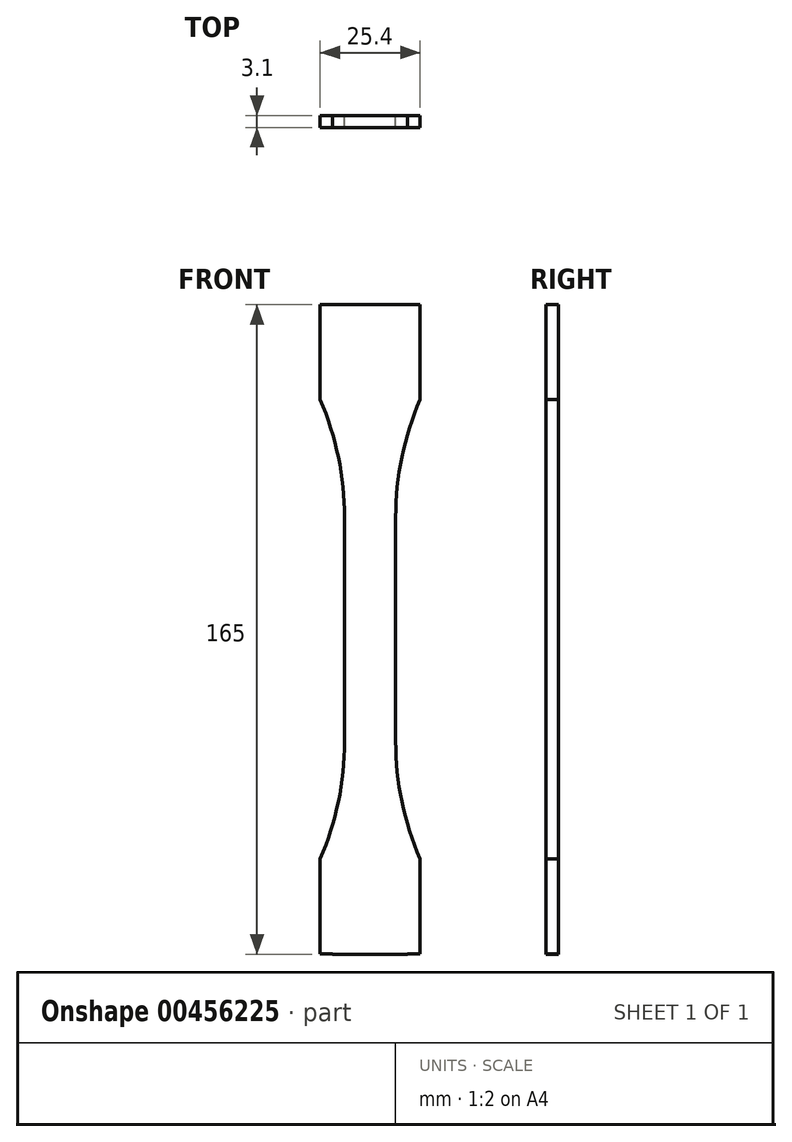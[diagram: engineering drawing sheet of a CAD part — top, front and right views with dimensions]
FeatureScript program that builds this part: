
annotation { "Feature Type Name" : "Feature", "Feature Type Description" : "" }
export const myFeature = defineFeature(function(context is Context, id is Id, definition is map)
    precondition{}
    {
        {
            var Q0;
            Q0=qCreatedBy(makeId("Front.planeOp"),FACE);
            var sketch = newSketch(context, id + "F0", { "sketchPlane" : qUnion([Q0])});
            skLineSegment(sketch, "E0.bottom", {"start": v(-6.5, 28.5) * mm, "end": v(0, 28.5) * mm});
            skLineSegment(sketch, "E0.top", {"start": v(-6.5, 0) * mm, "end": v(0, 0) * mm});
            skLineSegment(sketch, "E0.left", {"start": v(-6.5, 28.5) * mm, "end": v(-6.5, 0) * mm});
            skLineSegment(sketch, "E0.right", {"start": v(0, 28.5) * mm, "end": v(0, 0) * mm});
            skLineSegment(sketch, "E1", {"start": v(0, 28.5) * mm, "end": v(0, 49.5) * mm});
            skLineSegment(sketch, "E2.bottom", {"start": v(0, 49.5) * mm, "end": v(-9.5, 49.5) * mm});
            skLineSegment(sketch, "E2.top", {"start": v(0, 82.5) * mm, "end": v(-9.5, 82.5) * mm});
            skLineSegment(sketch, "E2.left", {"start": v(0, 49.5) * mm, "end": v(0, 82.5) * mm});
            skLineSegment(sketch, "E2.right", {"start": v(-9.5, 49.5) * mm, "end": v(-9.5, 49.5) * mm});
            skPoint(sketch, "E3.third.point", {"position": v(-81.94, 24.1) * mm});
            skPoint(sketch, "E4.third.point", {"position": v(-11.7, 28.5) * mm});
            skLineSegment(sketch, "E5", {"start": v(-9.5, 49.5) * mm, "end": v(-9.5, 82.5) * mm});
            skLineSegment(sketch, "E6.MirrorCS", {"start": v(9.5, 49.5) * mm, "end": v(9.5, 49.5) * mm});
            skLineSegment(sketch, "E7.MirrorCS", {"start": v(0, 82.5) * mm, "end": v(9.5, 82.5) * mm});
            skLineSegment(sketch, "E8.MirrorCS", {"start": v(6.5, 28.5) * mm, "end": v(6.5, 0) * mm});
            skLineSegment(sketch, "E9.MirrorCS", {"start": v(6.5, 28.5) * mm, "end": v(0, 28.5) * mm});
            skLineSegment(sketch, "E10.MirrorCS", {"start": v(0, 49.5) * mm, "end": v(0, 49.5) * mm});
            skLineSegment(sketch, "E11.MirrorCS", {"start": v(9.5, 49.5) * mm, "end": v(9.5, 82.5) * mm});
            skLineSegment(sketch, "E12.MirrorCS", {"start": v(6.5, 0) * mm, "end": v(0, 0) * mm});
            skLineSegment(sketch, "E13.MirrorCS", {"start": v(0, -28.5) * mm, "end": v(0, -49.5) * mm});
            skLineSegment(sketch, "E14.MirrorCS", {"start": v(0, -28.5) * mm, "end": v(0, 0) * mm});
            skLineSegment(sketch, "E15.MirrorCS", {"start": v(-9.5, -49.5) * mm, "end": v(-9.5, -49.5) * mm});
            skLineSegment(sketch, "E16.MirrorCS", {"start": v(0, -82.5) * mm, "end": v(9.5, -82.5) * mm});
            skLineSegment(sketch, "E17.MirrorCS", {"start": v(0, -49.5) * mm, "end": v(9.5, -49.5) * mm});
            skLineSegment(sketch, "E18.MirrorCS", {"start": v(-9.5, -49.5) * mm, "end": v(-9.5, -82.5) * mm});
            skLineSegment(sketch, "E19.MirrorCS", {"start": v(-6.5, -28.5) * mm, "end": v(-6.5, 0) * mm});
            skLineSegment(sketch, "E20.MirrorCS", {"start": v(-6.5, -28.5) * mm, "end": v(0, -28.5) * mm});
            skLineSegment(sketch, "E21.MirrorCS", {"start": v(0, -28.5) * mm, "end": v(0, -55.7) * mm});
            skLineSegment(sketch, "E22.MirrorCS", {"start": v(6.5, -28.5) * mm, "end": v(6.5, 0) * mm});
            skLineSegment(sketch, "E23.MirrorCS", {"start": v(9.5, -49.5) * mm, "end": v(9.5, -49.5) * mm});
            skLineSegment(sketch, "E24.MirrorCS", {"start": v(0, -82.5) * mm, "end": v(-9.5, -82.5) * mm});
            skLineSegment(sketch, "E25.MirrorCS", {"start": v(9.5, -49.5) * mm, "end": v(9.5, -82.5) * mm});
            skLineSegment(sketch, "E26.MirrorCS", {"start": v(6.5, -28.5) * mm, "end": v(0, -28.5) * mm});
            skLineSegment(sketch, "E27.MirrorCS", {"start": v(0, -49.5) * mm, "end": v(0, -82.5) * mm});
            skLineSegment(sketch, "E28.MirrorCS", {"start": v(0, -49.5) * mm, "end": v(-9.5, -49.5) * mm});
            skLineSegment(sketch, "E29", {"start": v(-9.5, 82.5) * mm, "end": v(-9.5, -82.5) * mm, "construction": true});
            skLineSegment(sketch, "E30", {"start": v(0, 82.5) * mm, "end": v(0, 28.5) * mm});
            skArc(sketch, "E31", {"start": v(-6.5, 28.5) * mm, "mid": v(-7.25, 39.1) * mm, "end": v(-9.5, 49.5) * mm});
            skArc(sketch, "E32.MirrorCS", {"start": v(6.5, 28.5) * mm, "mid": v(7.25, 39.1) * mm, "end": v(9.5, 49.5) * mm});
            skArc(sketch, "E33.MirrorCS", {"start": v(-6.5, -28.5) * mm, "mid": v(-7.25, -39.1) * mm, "end": v(-9.5, -49.5) * mm});
            skArc(sketch, "E34.MirrorCS", {"start": v(6.5, -28.5) * mm, "mid": v(7.25, -39.1) * mm, "end": v(9.5, -49.5) * mm});
            skPoint(sketch, "E35.third.point", {"position": v(-144.02, -12.93) * mm});
            skLineSegment(sketch, "E36.top", {"start": v(0, 82.5) * mm, "end": v(-12.7, 82.5) * mm});
            skPoint(sketch, "E37", {"position": v(-12.7, 58.36) * mm});
            skLineSegment(sketch, "E38", {"start": v(-12.7, 58.36) * mm, "end": v(-12.7, 82.5) * mm});
            skLineSegment(sketch, "E39", {"start": v(-12.7, 58.36) * mm, "end": v(-12.7, 58.36) * mm});
            skArc(sketch, "E40", {"start": v(-9.5, 49.5) * mm, "mid": v(-10.96, 53.98) * mm, "end": v(-12.7, 58.36) * mm});
            skLineSegment(sketch, "E41", {"start": v(0, 49.5) * mm, "end": v(9.5, 49.5) * mm});
            skArc(sketch, "E42.MirrorCS", {"start": v(9.5, 49.5) * mm, "mid": v(10.96, 53.98) * mm, "end": v(12.7, 58.36) * mm});
            skLineSegment(sketch, "E43.MirrorCS", {"start": v(12.7, 58.36) * mm, "end": v(12.7, 82.5) * mm});
            skLineSegment(sketch, "E44.MirrorCS", {"start": v(0, 82.5) * mm, "end": v(12.7, 82.5) * mm});
            skLineSegment(sketch, "E45.MirrorCS", {"start": v(0, -49.5) * mm, "end": v(0, -49.5) * mm});
            skLineSegment(sketch, "E46.MirrorCS", {"start": v(-12.7, -58.36) * mm, "end": v(-12.7, -58.36) * mm});
            skLineSegment(sketch, "E47.MirrorCS", {"start": v(0, -82.5) * mm, "end": v(12.7, -82.5) * mm});
            skLineSegment(sketch, "E48.MirrorCS", {"start": v(-12.7, -58.36) * mm, "end": v(-12.7, -82.5) * mm});
            skPoint(sketch, "E49.MirrorP", {"position": v(-12.7, -58.36) * mm});
            skLineSegment(sketch, "E50.MirrorCS", {"start": v(12.7, -58.36) * mm, "end": v(12.7, -82.5) * mm});
            skLineSegment(sketch, "E51.MirrorCS", {"start": v(0, -82.5) * mm, "end": v(-12.7, -82.5) * mm});
            skArc(sketch, "E52.MirrorCS", {"start": v(-9.5, -49.5) * mm, "mid": v(-10.96, -53.98) * mm, "end": v(-12.7, -58.36) * mm});
            skArc(sketch, "E53.MirrorCS", {"start": v(9.5, -49.5) * mm, "mid": v(10.96, -53.98) * mm, "end": v(12.7, -58.36) * mm});
            skSolve(sketch);
        }
        {
            var Q0;
            Q0 = qSketchRegion(id + "F0", true);
            extrude(context, id + "F1", {"entities" : qUnion([Q0]), "depth" : 3.1 * mm});
        }
        {
            var Q0;
            Q0 = qSketchRegion(id + "F0", true);
            extrude(context, id + "F2", {"entities" : qUnion([Q0]), "depth" : 3.1 * mm});
        }
    });
